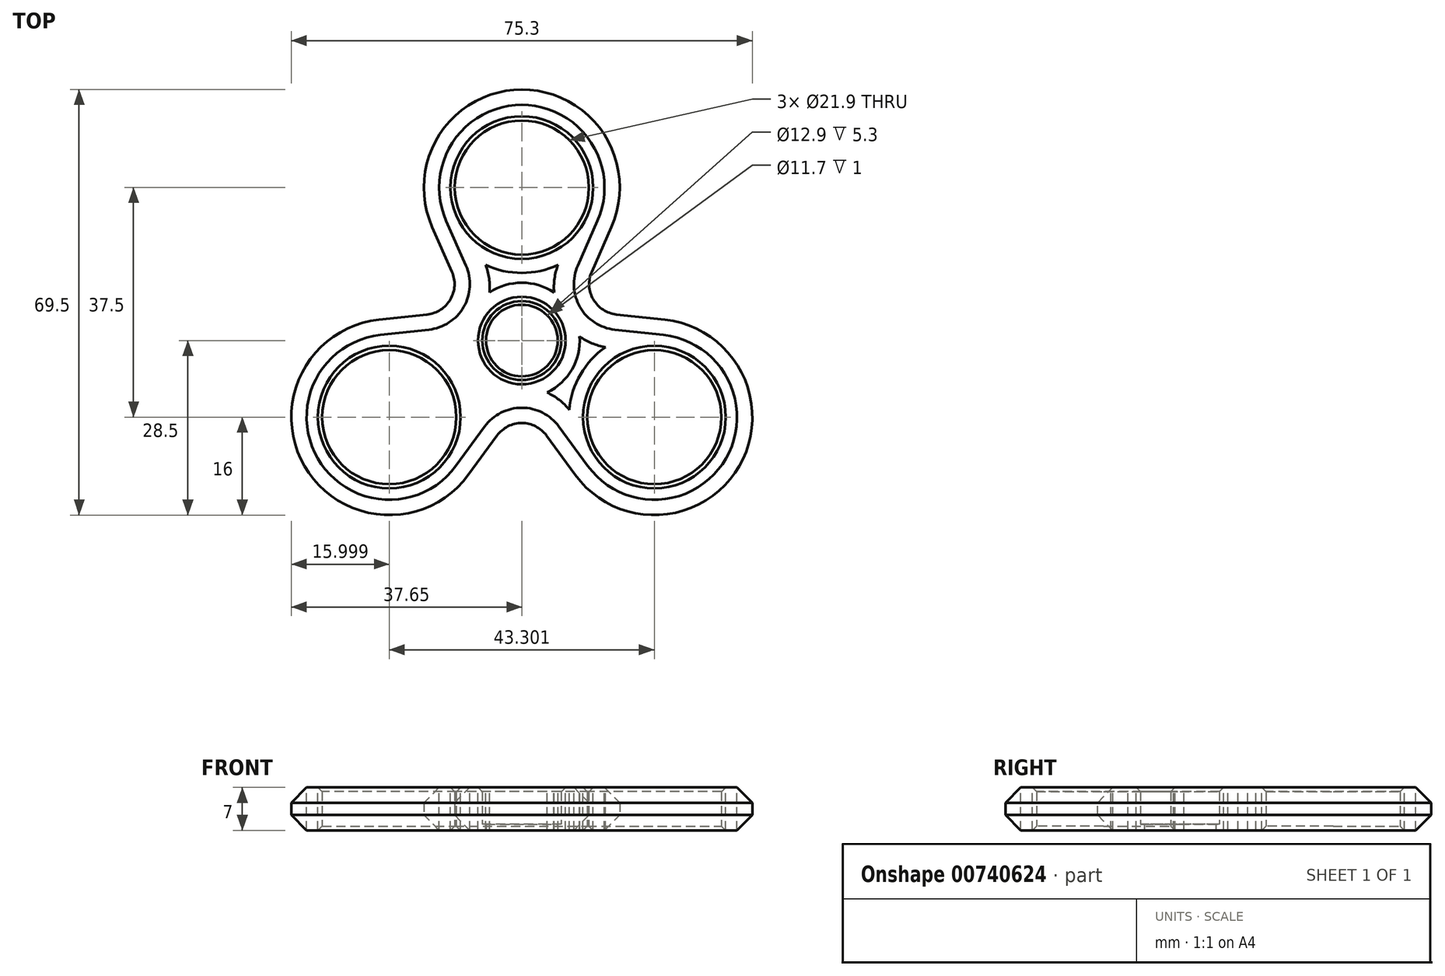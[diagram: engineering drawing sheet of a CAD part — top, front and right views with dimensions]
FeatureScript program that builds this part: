
annotation { "Feature Type Name" : "Feature", "Feature Type Description" : "" }
export const myFeature = defineFeature(function(context is Context, id is Id, definition is map)
    precondition{}
    {
        {
            var Q0;
            Q0=qCreatedBy(makeId("Top.planeOp"),FACE);
            var sketch = newSketch(context, id + "F0", { "sketchPlane" : qUnion([Q0])});
            skLineSegment(sketch, "E0", {"start": v(0, 0) * mm, "end": v(0, 25) * mm, "construction": true});
            skCircle(sketch, "E1", {"center": v(0, 25) * mm, "radius": 10.95 * mm});
            skArc(sketch, "E2", {"start": v(14.64, 18.54) * mm, "mid": v(0, 41) * mm, "end": v(-14.64, 18.54) * mm});
            skCircle(sketch, "E3", {"center": v(0, 0) * mm, "radius": 6.45 * mm});
            skArc(sketch, "E4.1.2", {"start": v(-23.37, 3.4) * mm, "mid": v(-35.5, -20.5) * mm, "end": v(-8.74, -21.95) * mm});
            skCircle(sketch, "E4.1.3", {"center": v(-21.65, -12.5) * mm, "radius": 10.95 * mm});
            skArc(sketch, "E4.2.2", {"start": v(8.74, -21.95) * mm, "mid": v(35.5, -20.5) * mm, "end": v(23.37, 3.4) * mm});
            skCircle(sketch, "E4.2.3", {"center": v(21.65, -12.5) * mm, "radius": 10.95 * mm});
            skLineSegment(sketch, "E5", {"start": v(0, 0) * mm, "end": v(-21.65, -12.5) * mm, "construction": true});
            skLineSegment(sketch, "E6", {"start": v(0, 0) * mm, "end": v(21.65, -12.5) * mm, "construction": true});
            skCircle(sketch, "E7", {"center": v(0, 0) * mm, "radius": 10 * mm, "construction": true});
            skLineSegment(sketch, "E8", {"start": v(0, 0) * mm, "end": v(-18.49, 10.67) * mm, "construction": true});
            skLineSegment(sketch, "E9", {"start": v(0, 0) * mm, "end": v(19.4, 11.2) * mm, "construction": true});
            skLineSegment(sketch, "E10", {"start": v(0, 0) * mm, "end": v(0, -30.9) * mm, "construction": true});
            skLineSegment(sketch, "E11", {"start": v(0, -10) * mm, "end": v(8.74, -21.95) * mm});
            skLineSegment(sketch, "E12", {"start": v(-14.64, 18.54) * mm, "end": v(-8.66, 5) * mm});
            skLineSegment(sketch, "E13", {"start": v(14.64, 18.54) * mm, "end": v(8.66, 5) * mm});
            skLineSegment(sketch, "E14", {"start": v(8.66, 5) * mm, "end": v(23.37, 3.4) * mm});
            skLineSegment(sketch, "E15", {"start": v(-23.37, 3.4) * mm, "end": v(-8.66, 5) * mm});
            skLineSegment(sketch, "E16", {"start": v(-8.74, -21.95) * mm, "end": v(0, -10) * mm});
            skSolve(sketch);
        }
        {
            var Q0;
            Q0=qSketchRegion(id+"F0",true);
            extrude(context, id + "F1", {"entities" : qUnion([Q0]), "depth" : 7 * mm, "offsetDistance" : 25 * mm});
        }
        {
            var Q0;
            Q0=makeQuery(id+"F1.opExtrude","SWEPT_EDGE",EDGE,{"disambiguationData":[OSD([sQuery(id+"F0.wireOp",EDGE,"hYaDFHxH-SQ1h-cJ0F-NxPf-ypNw5k6PqgM9"),sQuery(id+"F0.wireOp",EDGE,"E4.1.2")])]});
            var Q1;
            Q1=makeQuery(id+"F1.opExtrude","SWEPT_EDGE",EDGE,{"disambiguationData":[OSD([sQuery(id+"F0.wireOp",EDGE,"hYaDFHxH-SQ1h-cJ0F-NxPf-ypNw5k6PqgM9"),sQuery(id+"F0.wireOp",EDGE,"E4.2.2")])]});
            var Q2;
            Q2=makeQuery(id+"F1.opExtrude","SWEPT_EDGE",EDGE,{"disambiguationData":[OSD([sQuery(id+"F0.wireOp",EDGE,"E4.2.2"),sQuery(id+"F0.wireOp",EDGE,"79da703c-30cb-4167-bd47-66bc16433dd5.trimOffspring")])]});
            var Q3;
            Q3=makeQuery(id+"F1.opExtrude","SWEPT_EDGE",EDGE,{"disambiguationData":[OSD([sQuery(id+"F0.wireOp",EDGE,"E2"),sQuery(id+"F0.wireOp",EDGE,"79da703c-30cb-4167-bd47-66bc16433dd5.trimOffspring")])]});
            var Q4;
            Q4=makeQuery(id+"F1.opExtrude","SWEPT_EDGE",EDGE,{"disambiguationData":[OSD([sQuery(id+"F0.wireOp",EDGE,"E2"),sQuery(id+"F0.wireOp",EDGE,"007a9c35-0cf0-4482-a21c-6fcd3d696d74.trimOffspring")])]});
            var Q5;
            Q5=makeQuery(id+"F1.opExtrude","SWEPT_EDGE",EDGE,{"disambiguationData":[OSD([sQuery(id+"F0.wireOp",EDGE,"E4.1.2"),sQuery(id+"F0.wireOp",EDGE,"007a9c35-0cf0-4482-a21c-6fcd3d696d74.trimOffspring")])]});
            var Q6;
            Q6=makeQuery(id+"F1.opExtrude","SWEPT_EDGE",EDGE,{"disambiguationData":[OSD([sQuery(id+"F0.wireOp",EDGE,"ko7YyKQN-v9HZ-TaP5-rlhh-JDPldfvfd3NA"),sQuery(id+"F0.wireOp",EDGE,"E11")])]});
            var Q7;
            Q7=makeQuery(id+"F1.opExtrude","SWEPT_EDGE",EDGE,{"disambiguationData":[OSD([sQuery(id+"F0.wireOp",EDGE,"E13"),sQuery(id+"F0.wireOp",EDGE,"ksaeEowJ-kkjK-LKTK-lz2Y-0PddznCG0J7x")])]});
            var Q8;
            Q8=makeQuery(id+"F1.opExtrude","SWEPT_EDGE",EDGE,{"disambiguationData":[OSD([sQuery(id+"F0.wireOp",EDGE,"E12"),sQuery(id+"F0.wireOp",EDGE,"UxPp5yaT-IkeL-iCmG-1cEm-yVI7vS4TBKel")])]});
            fillet(context, id + "F2", {"entities" : qUnion([Q0, Q1, Q2, Q3, Q4, Q5, Q6, Q7, Q8]), "radius" : 5 * mm, "tangentPropagation" : true, "allowEdgeOverflow" : false});
        }
        {
            var Q0;
            Q0=makeQuery(id+"F1.opExtrude","CAP_EDGE",EDGE,{"disambiguationData":[OSD([sQuery(id+"F0.wireOp",EDGE,"E15")])],"isStart":false});
            var Q1;
            Q1=makeQuery(id+"F1.opExtrude","CAP_EDGE",EDGE,{"disambiguationData":[OSD([sQuery(id+"F0.wireOp",EDGE,"E16")])],"isStart":true});
            chamfer(context, id + "F3", {"entities" : qUnion([Q0, Q1]), "width" : 2.5 * mm, "tangentPropagation" : true});
        }
        {
            var Q0;
            Q0=makeQuery(id+"F1.opExtrude","CAP_FACE",FACE,{"disambiguationData":[OSD([sQuery(id+"F0.wireOp",EDGE,"E1"),sQuery(id+"F0.wireOp",EDGE,"E2"),sQuery(id+"F0.wireOp",EDGE,"E3"),sQuery(id+"F0.wireOp",EDGE,"E4.1.2"),sQuery(id+"F0.wireOp",EDGE,"E4.1.3"),sQuery(id+"F0.wireOp",EDGE,"E4.2.2"),sQuery(id+"F0.wireOp",EDGE,"E4.2.3"),sQuery(id+"F0.wireOp",EDGE,"E11"),sQuery(id+"F0.wireOp",EDGE,"E12"),sQuery(id+"F0.wireOp",EDGE,"E13"),sQuery(id+"F0.wireOp",EDGE,"E14"),sQuery(id+"F0.wireOp",EDGE,"E15"),sQuery(id+"F0.wireOp",EDGE,"E16")])],"isStart":true});
            var sketch = newSketch(context, id + "F4", { "sketchPlane" : qUnion([Q0])});
            skCircle(sketch, "E17.0", {"center": v(0, 0) * mm, "radius": 6.45 * mm});
            skCircle(sketch, "E18", {"center": v(0, 0) * mm, "radius": 5.85 * mm});
            skSolve(sketch);
        }
        {
            var Q0;
            Q0 = qSketchRegion(id + "F4", true);
            extrude(context, id + "F5", {"entities" : qUnion([Q0]), "operationType" : NewBodyOperationType.ADD, "oppositeDirection" : true, "depth" : 1 * mm, "offsetDistance" : 25 * mm});
        }
        {
            var Q0;
            Q0=makeQuery(id+"F1.opExtrude","CAP_EDGE",EDGE,{"disambiguationData":[OSD([sQuery(id+"F0.wireOp",EDGE,"E3")])],"isStart":false});
            var Q1;
            Q1=makeQuery(id+"F1.opExtrude","CAP_EDGE",EDGE,{"disambiguationData":[OSD([sQuery(id+"F0.wireOp",EDGE,"E4.1.3")])],"isStart":false});
            var Q2;
            Q2=makeQuery(id+"F1.opExtrude","CAP_EDGE",EDGE,{"disambiguationData":[OSD([sQuery(id+"F0.wireOp",EDGE,"E4.2.3")])],"isStart":false});
            var Q3;
            Q3=makeQuery(id+"F1.opExtrude","CAP_EDGE",EDGE,{"disambiguationData":[OSD([sQuery(id+"F0.wireOp",EDGE,"E1")])],"isStart":false});
            var Q4;
            Q4=makeQuery(id+"F1.opExtrude","CAP_EDGE",EDGE,{"disambiguationData":[OSD([sQuery(id+"F0.wireOp",EDGE,"E4.1.3")])],"isStart":true});
            var Q5;
            Q5=makeQuery(id+"F1.opExtrude","CAP_EDGE",EDGE,{"disambiguationData":[OSD([sQuery(id+"F0.wireOp",EDGE,"E4.2.3")])],"isStart":true});
            var Q6;
            Q6=makeQuery(id+"F1.opExtrude","CAP_EDGE",EDGE,{"disambiguationData":[OSD([sQuery(id+"F0.wireOp",EDGE,"E1")])],"isStart":true});
            chamfer(context, id + "F6", {"entities" : qUnion([Q0, Q1, Q2, Q3, Q4, Q5, Q6]), "width" : .7 * mm, "tangentPropagation" : true});
        }
        {
            var Q0;
            Q0=makeQuery(id+"F1.opExtrude","CAP_FACE",FACE,{"disambiguationData":[OSD([sQuery(id+"F0.wireOp",EDGE,"E1"),sQuery(id+"F0.wireOp",EDGE,"E3"),sQuery(id+"F0.wireOp",EDGE,"E4.1.3"),sQuery(id+"F0.wireOp",EDGE,"E4.2.3"),sQuery(id+"F0.wireOp",EDGE,"E11"),sQuery(id+"F0.wireOp",EDGE,"E12"),sQuery(id+"F0.wireOp",EDGE,"E13"),sQuery(id+"F0.wireOp",EDGE,"E14"),sQuery(id+"F0.wireOp",EDGE,"E15"),sQuery(id+"F0.wireOp",EDGE,"E16"),sQuery(id+"F0.wireOp",EDGE,"E2"),sQuery(id+"F0.wireOp",EDGE,"E4.2.2"),sQuery(id+"F0.wireOp",EDGE,"E4.1.2")])],"isStart":false});
            var sketch = newSketch(context, id + "F7", { "sketchPlane" : qUnion([Q0])});
            skArc(sketch, "E19.0", {"start": v(-6.05, -14.04) * mm, "mid": v(0, -10.97) * mm, "end": v(6.05, -14.04) * mm, "construction": true});
            skArc(sketch, "E19.2", {"start": v(15.19, 1.78) * mm, "mid": v(9.5, 5.49) * mm, "end": v(9.13, 12.26) * mm, "construction": true});
            skArc(sketch, "E20", {"start": v(-9.43, 0.65) * mm, "mid": v(-8.18, -4.72) * mm, "end": v(-4.15, -8.5) * mm});
            skArc(sketch, "E21", {"start": v(-7.75, -11.3) * mm, "mid": v(-9.57, -5.52) * mm, "end": v(-13.66, -1.06) * mm});
            skArc(sketch, "E22.1", {"start": v(-9.43, 0.65) * mm, "mid": v(-11.45, -0.44) * mm, "end": v(-13.66, -1.06) * mm});
            skLineSegment(sketch, "E23", {"start": v(0, 0) * mm, "end": v(-21.65, -12.5) * mm, "construction": true});
            skLineSegment(sketch, "E24", {"start": v(0, 0) * mm, "end": v(-15.32, 9.1) * mm, "construction": true});
            skArc(sketch, "E25.MirrorCS", {"start": v(-4.15, -8.5) * mm, "mid": v(-6.1, -9.7) * mm, "end": v(-7.75, -11.3) * mm});
            skArc(sketch, "E26.1.0", {"start": v(4.15, -8.5) * mm, "mid": v(6.1, -9.7) * mm, "end": v(7.75, -11.3) * mm});
            skArc(sketch, "E26.1.1", {"start": v(13.66, -1.06) * mm, "mid": v(9.57, -5.53) * mm, "end": v(7.75, -11.3) * mm});
            skArc(sketch, "E26.1.2", {"start": v(4.15, -8.5) * mm, "mid": v(8.18, -4.73) * mm, "end": v(9.43, 0.65) * mm});
            skArc(sketch, "E26.1.3", {"start": v(9.43, 0.65) * mm, "mid": v(11.45, -0.44) * mm, "end": v(13.66, -1.06) * mm});
            skArc(sketch, "E26.2.0", {"start": v(5.28, 7.84) * mm, "mid": v(5.34, 10.14) * mm, "end": v(5.91, 12.36) * mm});
            skArc(sketch, "E26.2.1", {"start": v(-5.91, 12.36) * mm, "mid": v(0, 11.05) * mm, "end": v(5.91, 12.36) * mm});
            skArc(sketch, "E26.2.2", {"start": v(5.28, 7.84) * mm, "mid": v(0, 9.45) * mm, "end": v(-5.28, 7.84) * mm});
            skArc(sketch, "E26.2.3", {"start": v(-5.28, 7.84) * mm, "mid": v(-5.34, 10.14) * mm, "end": v(-5.91, 12.36) * mm});
            skSolve(sketch);
        }
        {
            var Q0;
            Q0=makeQuery(id+"F7.imprint","IMPRINT",FACE,{"disambiguationData":[TD([[makeQuery(id+"F7.imprint","IMPRINT",EDGE,{"derivedFrom":sQuery(id+"F7.wireOp",EDGE,"E20")}),-1.0]])]});
            var Q1;
            Q1=makeQuery(id+"F7.imprint","IMPRINT",FACE,{"disambiguationData":[TD([[makeQuery(id+"F7.imprint","IMPRINT",EDGE,{"derivedFrom":sQuery(id+"F7.wireOp",EDGE,"E26.2.0")}),1.0]])]});
            var Q2;
            Q2=makeQuery(id+"F7.imprint","IMPRINT",FACE,{"disambiguationData":[TD([[makeQuery(id+"F7.imprint","IMPRINT",EDGE,{"derivedFrom":sQuery(id+"F7.wireOp",EDGE,"E26.1.0")}),1.0]])]});
            extrude(context, id + "F8", {"entities" : qUnion([Q0, Q1, Q2]), "operationType" : NewBodyOperationType.REMOVE, "oppositeDirection" : true, "depth" : 25 * mm, "offsetDistance" : 25 * mm});
        }
    });
